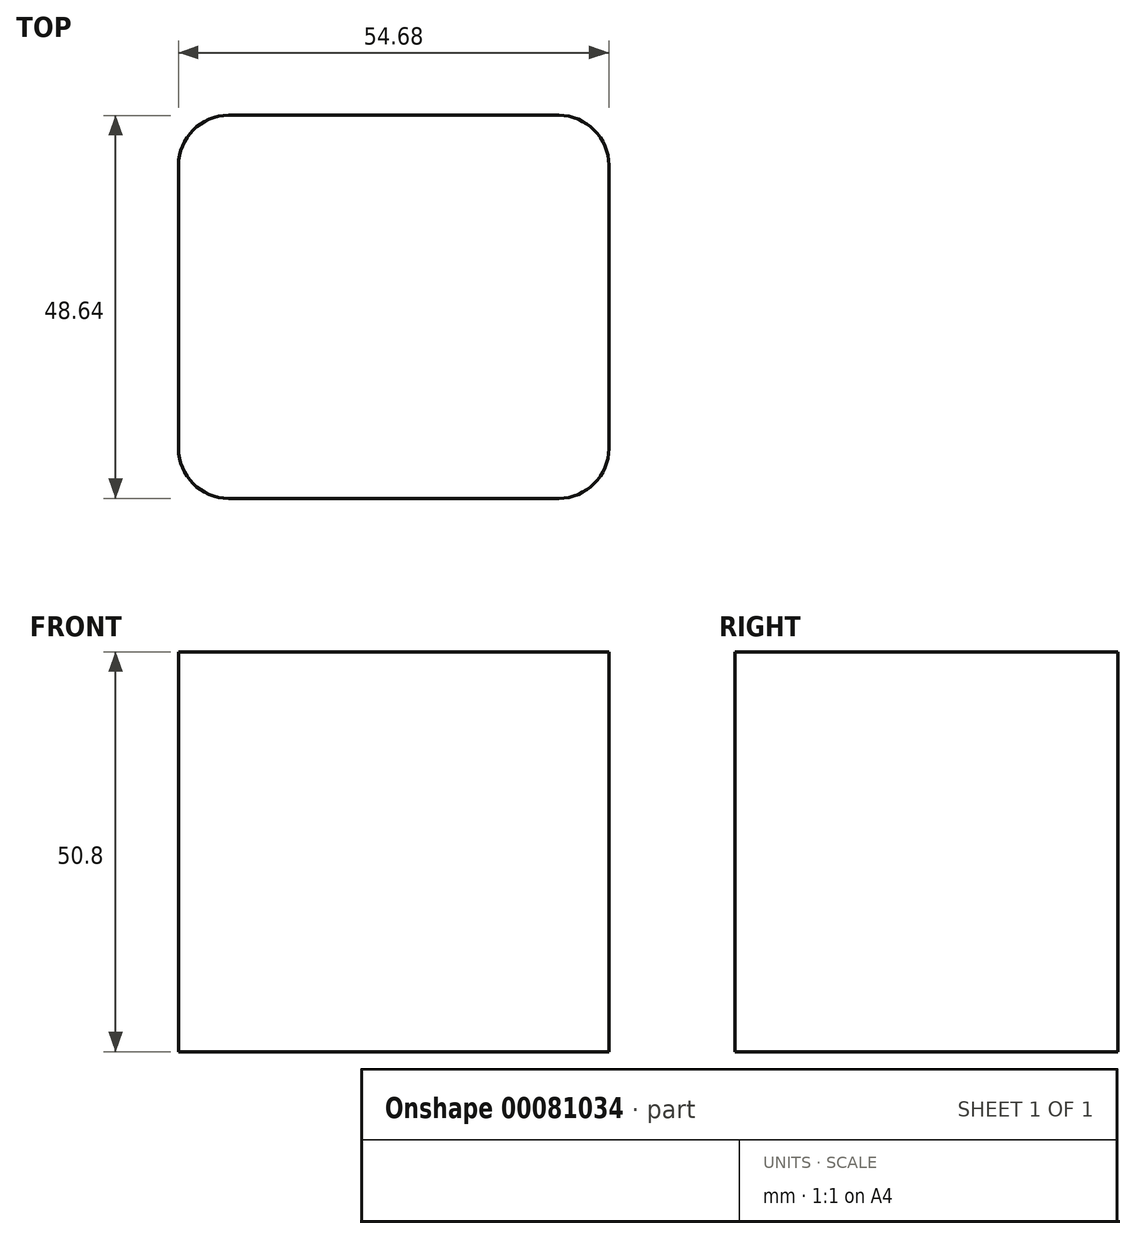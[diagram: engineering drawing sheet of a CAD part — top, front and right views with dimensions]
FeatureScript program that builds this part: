
annotation { "Feature Type Name" : "Feature", "Feature Type Description" : "" }
export const myFeature = defineFeature(function(context is Context, id is Id, definition is map)
    precondition{}
    {
        {
            var Q0;
            Q0=qCreatedBy(makeId("Top.planeOp"),FACE);
            var sketch = newSketch(context, id + "F0", { "sketchPlane" : qUnion([Q0])});
            skLineSegment(sketch, "E0.bottom", {"start": v(20.99, 24.32) * mm, "end": v(-20.99, 24.32) * mm});
            skLineSegment(sketch, "E0.top", {"start": v(20.99, -24.32) * mm, "end": v(-20.99, -24.32) * mm});
            skLineSegment(sketch, "E0.left", {"start": v(27.34, 17.97) * mm, "end": v(27.34, -17.97) * mm});
            skLineSegment(sketch, "E0.right", {"start": v(-27.34, 17.97) * mm, "end": v(-27.34, -17.97) * mm});
            skPoint(sketch, "E0.middle", {"position": v(0, 0) * mm});
            skPoint(sketch, "E1.visualSharp", {"position": v(-27.34, 24.32) * mm});
            skArc(sketch, "E1.filletArc", {"start": v(-20.99, 24.32) * mm, "mid": v(-25.48, 22.46) * mm, "end": v(-27.34, 17.97) * mm});
            skPoint(sketch, "E2.visualSharp", {"position": v(27.34, 24.32) * mm});
            skArc(sketch, "E2.filletArc", {"start": v(27.34, 17.97) * mm, "mid": v(25.48, 22.46) * mm, "end": v(20.99, 24.32) * mm});
            skPoint(sketch, "E3.visualSharp", {"position": v(27.34, -24.32) * mm});
            skArc(sketch, "E3.filletArc", {"start": v(20.99, -24.32) * mm, "mid": v(25.48, -22.46) * mm, "end": v(27.34, -17.97) * mm});
            skPoint(sketch, "E4.visualSharp", {"position": v(-27.34, -24.32) * mm});
            skArc(sketch, "E4.filletArc", {"start": v(-27.34, -17.97) * mm, "mid": v(-25.48, -22.46) * mm, "end": v(-20.99, -24.32) * mm});
            skSolve(sketch);
        }
        {
            var Q0;
            Q0=makeQuery(id+"F0.imprint","IMPRINT",FACE,{"disambiguationData":[TD([[makeQuery(id+"F0.imprint","IMPRINT",EDGE,{"derivedFrom":sQuery(id+"F0.wireOp",EDGE,"E0.bottom")}),1.0]])]});
            extrude(context, id + "F1", {"entities" : qUnion([Q0]), "depth" : 50.8 * mm});
        }
    });
